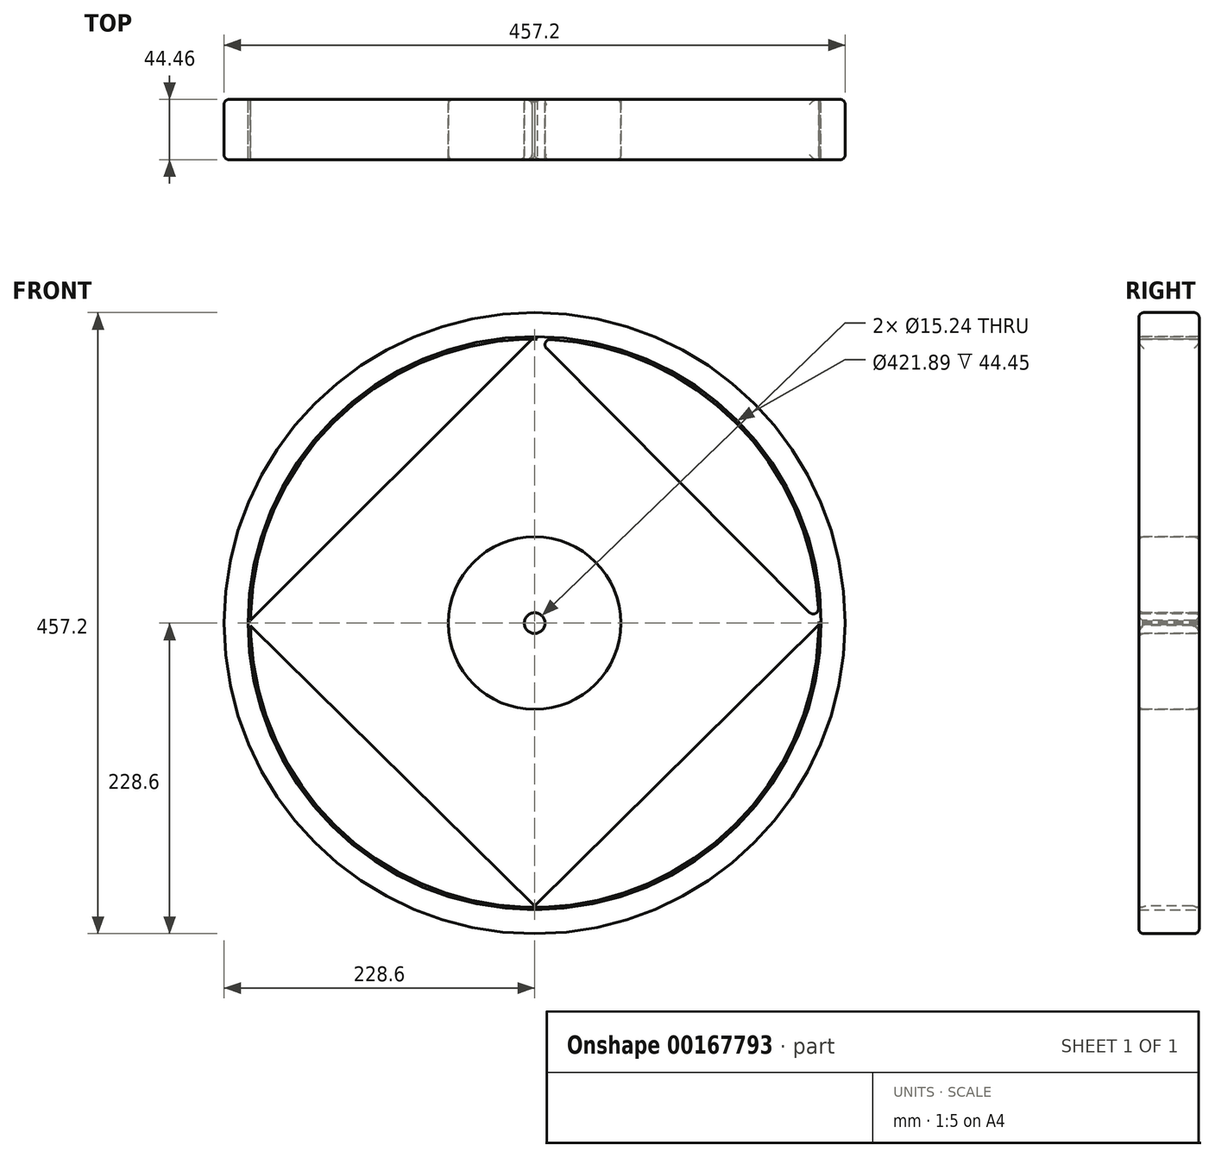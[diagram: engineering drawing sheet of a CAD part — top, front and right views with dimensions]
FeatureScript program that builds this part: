
annotation { "Feature Type Name" : "Feature", "Feature Type Description" : "" }
export const myFeature = defineFeature(function(context is Context, id is Id, definition is map)
    precondition{}
    {
        {
            var Q0;
            Q0=qCreatedBy(makeId("Front.planeOp"),FACE);
            var sketch = newSketch(context, id + "F0", { "sketchPlane" : qUnion([Q0])});
            skCircle(sketch, "E0", {"center": v(0, 0) * mm, "radius": 228.6 * mm});
            skCircle(sketch, "E1", {"center": v(0, 0) * mm, "radius": 7.62 * mm});
            skLineSegment(sketch, "E2", {"start": v(0, 0) * mm, "end": v(0, 228.6) * mm});
            skLineSegment(sketch, "E3", {"start": v(0, 0) * mm, "end": v(0, -228.6) * mm});
            skLineSegment(sketch, "E4", {"start": v(0, 0) * mm, "end": v(-228.6, 0) * mm});
            skLineSegment(sketch, "E5", {"start": v(0, 0) * mm, "end": v(228.6, 0) * mm});
            skCircle(sketch, "E6", {"center": v(0, 0) * mm, "radius": 63.5 * mm});
            skCircle(sketch, "E7", {"center": v(0, 0) * mm, "radius": 210.95 * mm});
            skSolve(sketch);
        }
        {
            var Q0;
            Q0=qSketchRegion(id+"F0",true);
            var Q1;
            {var subQ0=sQuery(id+"F0.wireOp",EDGE,"E2");var subQ1=sQuery(id+"F0.wireOp",EDGE,"E0");var subQ2=makeQuery(id+"F0.imprint","INTERSECT",VERTEX,{"derivedFrom":[subQ1,subQ0]});Q1=makeQuery(id+"F0.imprint","IMPRINT",FACE,{"disambiguationData":[TD([[makeQuery(id+"F0.imprint","IMPRINT",EDGE,{"disambiguationData":[TD([[subQ2,-1.0]])],"derivedFrom":subQ1}),1.0]])]});}
            var Q2;
            {var subQ0=sQuery(id+"F0.wireOp",EDGE,"E2");var subQ1=sQuery(id+"F0.wireOp",EDGE,"E1");var subQ2=makeQuery(id+"F0.imprint","INTERSECT",VERTEX,{"derivedFrom":[subQ1,subQ0]});Q2=makeQuery(id+"F0.imprint","IMPRINT",FACE,{"disambiguationData":[TD([[makeQuery(id+"F0.imprint","IMPRINT",EDGE,{"disambiguationData":[TD([[subQ2,-1.0]])],"derivedFrom":subQ1}),-1.0]])]});}
            var Q3;
            {var subQ0=sQuery(id+"F0.wireOp",EDGE,"E2");var subQ1=sQuery(id+"F0.wireOp",EDGE,"E1");var subQ2=makeQuery(id+"F0.imprint","INTERSECT",VERTEX,{"derivedFrom":[subQ1,subQ0]});Q3=makeQuery(id+"F0.imprint","IMPRINT",FACE,{"disambiguationData":[TD([[makeQuery(id+"F0.imprint","IMPRINT",EDGE,{"disambiguationData":[TD([[subQ2,1.0]])],"derivedFrom":subQ1}),-1.0]])]});}
            var Q4;
            {var subQ0=sQuery(id+"F0.wireOp",EDGE,"E5");var subQ1=sQuery(id+"F0.wireOp",EDGE,"E1");var subQ2=makeQuery(id+"F0.imprint","INTERSECT",VERTEX,{"derivedFrom":[subQ1,subQ0]});Q4=makeQuery(id+"F0.imprint","IMPRINT",FACE,{"disambiguationData":[TD([[makeQuery(id+"F0.imprint","IMPRINT",EDGE,{"disambiguationData":[TD([[subQ2,1.0]])],"derivedFrom":subQ1}),-1.0]])]});}
            var Q5;
            {var subQ0=sQuery(id+"F0.wireOp",EDGE,"E4");var subQ1=sQuery(id+"F0.wireOp",EDGE,"E1");var subQ2=makeQuery(id+"F0.imprint","INTERSECT",VERTEX,{"derivedFrom":[subQ1,subQ0]});Q5=makeQuery(id+"F0.imprint","IMPRINT",FACE,{"disambiguationData":[TD([[makeQuery(id+"F0.imprint","IMPRINT",EDGE,{"disambiguationData":[TD([[subQ2,-1.0]])],"derivedFrom":subQ1}),-1.0]])]});}
            extrude(context, id + "F1", {"entities" : qUnion([Q0, Q1, Q2, Q3, Q4, Q5]), "endBound" : BoundingType.SYMMETRIC, "depth" : 44.45 * mm});
        }
        {
            var Q0;
            Q0=makeQuery(id+"F1.opExtrude","CAP_FACE",FACE,{"disambiguationData":[OSD([sQuery(id+"F0.wireOp",EDGE,"E1"),sQuery(id+"F0.wireOp",EDGE,"E6")])],"isStart":false});
            var sketch = newSketch(context, id + "F2", { "sketchPlane" : qUnion([Q0])});
            skLineSegment(sketch, "E8", {"start": v(-209.14, 0) * mm, "end": v(-211.01, 0) * mm});
            skLineSegment(sketch, "E9", {"start": v(209.14, 0) * mm, "end": v(210.23, 0) * mm});
            skLineSegment(sketch, "E10", {"start": v(0, 209.14) * mm, "end": v(0, 211.07) * mm});
            skLineSegment(sketch, "E11", {"start": v(0, -208.2) * mm, "end": v(-211.01, 0) * mm});
            skLineSegment(sketch, "E12", {"start": v(-211.01, 0) * mm, "end": v(0, 211.07) * mm});
            skLineSegment(sketch, "E13", {"start": v(0, 211.07) * mm, "end": v(210.23, 0) * mm});
            skLineSegment(sketch, "E14", {"start": v(210.23, 0) * mm, "end": v(0, -208.2) * mm});
            skCircle(sketch, "E15", {"center": v(0, 0) * mm, "radius": 209.14 * mm});
            skSolve(sketch);
        }
        {
            var Q0;
            {var subQ0=sQuery(id+"F2.wireOp",EDGE,"E14");var subQ1=sQuery(id+"F2.wireOp",EDGE,"E11");var subQ2=makeQuery(id+"F2.imprint","INTERSECT",VERTEX,{"derivedFrom":[subQ1,subQ0]});Q0=makeQuery(id+"F2.imprint","IMPRINT",FACE,{"disambiguationData":[TD([[makeQuery(id+"F2.imprint","IMPRINT",EDGE,{"disambiguationData":[TD([[subQ2,-1.0]])],"derivedFrom":subQ1}),1.0]])]});}
            var Q1;
            {var subQ0=sQuery(id+"F2.wireOp",EDGE,"E15");var subQ1=sQuery(id+"F2.wireOp",EDGE,"E12");var subQ2=makeQuery(id+"F2.imprint","INTERSECT",VERTEX,{"disambiguationData":[OD(0.0)],"derivedFrom":[subQ1,subQ0]});Q1=makeQuery(id+"F2.imprint","IMPRINT",FACE,{"disambiguationData":[TD([[makeQuery(id+"F2.imprint","IMPRINT",EDGE,{"disambiguationData":[TD([[subQ2,-1.0]])],"derivedFrom":subQ1}),1.0]])]});}
            var Q2;
            {var subQ0=sQuery(id+"F2.wireOp",EDGE,"E15");var subQ1=sQuery(id+"F2.wireOp",EDGE,"E13");var subQ2=makeQuery(id+"F2.imprint","INTERSECT",VERTEX,{"disambiguationData":[OD(0.0)],"derivedFrom":[subQ1,subQ0]});Q2=makeQuery(id+"F2.imprint","IMPRINT",FACE,{"disambiguationData":[TD([[makeQuery(id+"F2.imprint","IMPRINT",EDGE,{"disambiguationData":[TD([[subQ2,-1.0]])],"derivedFrom":subQ1}),1.0]])]});}
            var Q3;
            {var subQ0=sQuery(id+"F2.wireOp",EDGE,"E8");Q3=makeQuery(id+"F2.imprint","IMPRINT",FACE,{"disambiguationData":[TD([[makeQuery(id+"F2.imprint","IMPRINT",EDGE,{"derivedFrom":subQ0}),1.0]])]});}
            var Q4;
            {var subQ0=sQuery(id+"F2.wireOp",EDGE,"E8");Q4=makeQuery(id+"F2.imprint","IMPRINT",FACE,{"disambiguationData":[TD([[makeQuery(id+"F2.imprint","IMPRINT",EDGE,{"derivedFrom":subQ0}),-1.0]])]});}
            var Q5;
            {var subQ0=sQuery(id+"F2.wireOp",EDGE,"E9");Q5=makeQuery(id+"F2.imprint","IMPRINT",FACE,{"disambiguationData":[TD([[makeQuery(id+"F2.imprint","IMPRINT",EDGE,{"derivedFrom":subQ0}),1.0]])]});}
            var Q6;
            {var subQ0=sQuery(id+"F2.wireOp",EDGE,"E9");Q6=makeQuery(id+"F2.imprint","IMPRINT",FACE,{"disambiguationData":[TD([[makeQuery(id+"F2.imprint","IMPRINT",EDGE,{"derivedFrom":subQ0}),-1.0]])]});}
            var Q7;
            {var subQ0=sQuery(id+"F2.wireOp",EDGE,"E10");Q7=makeQuery(id+"F2.imprint","IMPRINT",FACE,{"disambiguationData":[TD([[makeQuery(id+"F2.imprint","IMPRINT",EDGE,{"derivedFrom":subQ0}),1.0]])]});}
            var Q8;
            {var subQ0=sQuery(id+"F2.wireOp",EDGE,"E10");Q8=makeQuery(id+"F2.imprint","IMPRINT",FACE,{"disambiguationData":[TD([[makeQuery(id+"F2.imprint","IMPRINT",EDGE,{"derivedFrom":subQ0}),-1.0]])]});}
            var Q9;
            Q9=makeQuery(id+"F2.imprint","IMPRINT",FACE,{"disambiguationData":[TD([[makeQuery(id+"F2.imprint","IMPRINT",EDGE,{"derivedFrom":makeQuery(id+"F1.opExtrude","CAP_EDGE",EDGE,{"disambiguationData":[OSD([sQuery(id+"F0.wireOp",EDGE,"E1")])],"isStart":false})}),-1.0]])]});
            extrude(context, id + "F3", {"entities" : qUnion([Q0, Q1, Q2, Q3, Q4, Q5, Q6, Q7, Q8, Q9]), "oppositeDirection" : true, "depth" : 44.45 * mm});
        }
        {
            var Q0;
            {var subQ0=sQuery(id+"F2.wireOp",EDGE,"E15");var subQ1=sQuery(id+"F2.wireOp",EDGE,"E13");Q0=makeQuery(id+"F3.opExtrude","SWEPT_EDGE",EDGE,{"disambiguationData":[OSD([subQ1,subQ0]),TDD([makeQuery(id+"F2.imprint","INTERSECT",VERTEX,{"disambiguationData":[OD(1.0)],"derivedFrom":[subQ1,subQ0]})]),ownerDisambiguation([makeQuery(id+"F3.opExtrude","SWEPT_BODY",BODY,{"disambiguationData":[OSD([subQ1,subQ0])]})])]});}
            var Q1;
            {var subQ0=sQuery(id+"F2.wireOp",EDGE,"E15");var subQ1=sQuery(id+"F2.wireOp",EDGE,"E13");Q1=makeQuery(id+"F3.opExtrude","SWEPT_EDGE",EDGE,{"disambiguationData":[OSD([subQ1,subQ0]),TDD([makeQuery(id+"F2.imprint","INTERSECT",VERTEX,{"disambiguationData":[OD(0.0)],"derivedFrom":[subQ1,subQ0]})]),ownerDisambiguation([makeQuery(id+"F3.opExtrude","SWEPT_BODY",BODY,{"disambiguationData":[OSD([subQ1,subQ0])]})])]});}
            var Q2;
            {var subQ0=sQuery(id+"F2.wireOp",EDGE,"E15");var subQ1=sQuery(id+"F2.wireOp",EDGE,"E11");Q2=makeQuery(id+"F3.opExtrude","SWEPT_EDGE",EDGE,{"disambiguationData":[OSD([subQ1,subQ0]),ownerDisambiguation([makeQuery(id+"F3.opExtrude","SWEPT_BODY",BODY,{"disambiguationData":[OSD([subQ1,sQuery(id+"F2.wireOp",EDGE,"E14"),subQ0])]})])]});}
            var Q3;
            Q3=makeQuery(id+"F3.opExtrude","SWEPT_EDGE",EDGE,{"disambiguationData":[OSD([sQuery(id+"F2.wireOp",EDGE,"E11"),sQuery(id+"F2.wireOp",EDGE,"E14")])]});
            var Q4;
            Q4=makeQuery(id+"F1.opExtrude","CAP_EDGE",EDGE,{"disambiguationData":[OSD([sQuery(id+"F0.wireOp",EDGE,"E6")])],"isStart":true});
            var Q5;
            Q5=makeQuery(id+"F3.opExtrude","CAP_EDGE",EDGE,{"disambiguationData":[OSD([sQuery(id+"F0.wireOp",EDGE,"E6")])],"isStart":true});
            var Q6;
            Q6=makeQuery(id+"F3.opExtrude","CAP_FACE",FACE,{"disambiguationData":[OSD([sQuery(id+"F0.wireOp",EDGE,"E6")])],"isStart":true});
            var Q7;
            Q7=makeQuery(id+"F1.opExtrude","CAP_EDGE",EDGE,{"disambiguationData":[OSD([sQuery(id+"F0.wireOp",EDGE,"E0")])],"isStart":false});
            var Q8;
            Q8=makeQuery(id+"F1.opExtrude","CAP_EDGE",EDGE,{"disambiguationData":[OSD([sQuery(id+"F0.wireOp",EDGE,"E0")])],"isStart":true});
            var Q9;
            {var subQ0=sQuery(id+"F2.wireOp",EDGE,"E15");var subQ1=sQuery(id+"F2.wireOp",EDGE,"E12");Q9=makeQuery(id+"F3.opExtrude","CAP_EDGE",EDGE,{"disambiguationData":[OSD([subQ1]),TDD([makeQuery(id+"F2.imprint","IMPRINT",EDGE,{"disambiguationData":[TD([[makeQuery(id+"F2.imprint","INTERSECT",VERTEX,{"disambiguationData":[OD(0.0)],"derivedFrom":[subQ1,subQ0]}),-1.0]])],"derivedFrom":subQ1})])],"isStart":true});}
            var Q10;
            {var subQ0=sQuery(id+"F2.wireOp",EDGE,"E15");var subQ1=sQuery(id+"F2.wireOp",EDGE,"E13");Q10=makeQuery(id+"F3.opExtrude","CAP_EDGE",EDGE,{"disambiguationData":[OSD([subQ1]),TDD([makeQuery(id+"F2.imprint","IMPRINT",EDGE,{"disambiguationData":[TD([[makeQuery(id+"F2.imprint","INTERSECT",VERTEX,{"disambiguationData":[OD(0.0)],"derivedFrom":[subQ1,subQ0]}),-1.0]])],"derivedFrom":subQ1})])],"isStart":true});}
            var Q11;
            {var subQ0=sQuery(id+"F2.wireOp",EDGE,"E14");Q11=makeQuery(id+"F3.opExtrude","CAP_EDGE",EDGE,{"disambiguationData":[OSD([subQ0]),TDD([makeQuery(id+"F2.imprint","IMPRINT",EDGE,{"disambiguationData":[TD([[makeQuery(id+"F2.imprint","INTERSECT",VERTEX,{"derivedFrom":[sQuery(id+"F2.wireOp",EDGE,"E11"),subQ0]}),1.0]])],"derivedFrom":subQ0})])],"isStart":true});}
            var Q12;
            {var subQ0=sQuery(id+"F2.wireOp",EDGE,"E11");Q12=makeQuery(id+"F3.opExtrude","CAP_EDGE",EDGE,{"disambiguationData":[OSD([subQ0]),TDD([makeQuery(id+"F2.imprint","IMPRINT",EDGE,{"disambiguationData":[TD([[makeQuery(id+"F2.imprint","INTERSECT",VERTEX,{"derivedFrom":[subQ0,sQuery(id+"F2.wireOp",EDGE,"E14")]}),-1.0]])],"derivedFrom":subQ0})])],"isStart":true});}
            var Q13;
            {var subQ0=sQuery(id+"F2.wireOp",EDGE,"E15");var subQ1=sQuery(id+"F2.wireOp",EDGE,"E13");Q13=makeQuery(id+"F3.opExtrude","CAP_EDGE",EDGE,{"disambiguationData":[OSD([subQ1]),TDD([makeQuery(id+"F2.imprint","IMPRINT",EDGE,{"disambiguationData":[TD([[makeQuery(id+"F2.imprint","INTERSECT",VERTEX,{"disambiguationData":[OD(0.0)],"derivedFrom":[subQ1,subQ0]}),-1.0]])],"derivedFrom":subQ1})])],"isStart":false});}
            var Q14;
            {var subQ0=sQuery(id+"F2.wireOp",EDGE,"E11");Q14=makeQuery(id+"F3.opExtrude","CAP_EDGE",EDGE,{"disambiguationData":[OSD([subQ0]),TDD([makeQuery(id+"F2.imprint","IMPRINT",EDGE,{"disambiguationData":[TD([[makeQuery(id+"F2.imprint","INTERSECT",VERTEX,{"derivedFrom":[subQ0,sQuery(id+"F2.wireOp",EDGE,"E14")]}),-1.0]])],"derivedFrom":subQ0})])],"isStart":false});}
            var Q15;
            {var subQ0=sQuery(id+"F2.wireOp",EDGE,"E14");Q15=makeQuery(id+"F3.opExtrude","CAP_EDGE",EDGE,{"disambiguationData":[OSD([subQ0]),TDD([makeQuery(id+"F2.imprint","IMPRINT",EDGE,{"disambiguationData":[TD([[makeQuery(id+"F2.imprint","INTERSECT",VERTEX,{"derivedFrom":[sQuery(id+"F2.wireOp",EDGE,"E11"),subQ0]}),1.0]])],"derivedFrom":subQ0})])],"isStart":false});}
            var Q16;
            {var subQ0=sQuery(id+"F2.wireOp",EDGE,"E15");var subQ1=sQuery(id+"F2.wireOp",EDGE,"E12");Q16=makeQuery(id+"F3.opExtrude","CAP_EDGE",EDGE,{"disambiguationData":[OSD([subQ1]),TDD([makeQuery(id+"F2.imprint","IMPRINT",EDGE,{"disambiguationData":[TD([[makeQuery(id+"F2.imprint","INTERSECT",VERTEX,{"disambiguationData":[OD(0.0)],"derivedFrom":[subQ1,subQ0]}),-1.0]])],"derivedFrom":subQ1})])],"isStart":false});}
            fillet(context, id + "F4", {"entities" : qUnion([Q0, Q1, Q2, Q3, Q4, Q5, Q6, Q7, Q8, Q9, Q10, Q11, Q12, Q13, Q14, Q15, Q16]), "radius" : 3.8 * mm, "tangentPropagation" : true, "allowEdgeOverflow" : false});
        }
        {
            var Q0;
            {var subQ0=sQuery(id+"F2.wireOp",EDGE,"E15");var subQ1=sQuery(id+"F2.wireOp",EDGE,"E13");Q0=makeQuery(id+"F3.opExtrude","CAP_EDGE",EDGE,{"disambiguationData":[OSD([subQ1]),TDD([makeQuery(id+"F2.imprint","IMPRINT",EDGE,{"disambiguationData":[TD([[makeQuery(id+"F2.imprint","INTERSECT",VERTEX,{"disambiguationData":[OD(0.0)],"derivedFrom":[subQ1,subQ0]}),-1.0]])],"derivedFrom":subQ1})])],"isStart":true});}
            var Q1;
            {var subQ0=sQuery(id+"F2.wireOp",EDGE,"E14");Q1=makeQuery(id+"F3.opExtrude","CAP_EDGE",EDGE,{"disambiguationData":[OSD([subQ0]),TDD([makeQuery(id+"F2.imprint","IMPRINT",EDGE,{"disambiguationData":[TD([[makeQuery(id+"F2.imprint","INTERSECT",VERTEX,{"derivedFrom":[sQuery(id+"F2.wireOp",EDGE,"E11"),subQ0]}),1.0]])],"derivedFrom":subQ0})])],"isStart":true});}
            var Q2;
            {var subQ0=sQuery(id+"F2.wireOp",EDGE,"E11");Q2=makeQuery(id+"F3.opExtrude","CAP_EDGE",EDGE,{"disambiguationData":[OSD([subQ0]),TDD([makeQuery(id+"F2.imprint","IMPRINT",EDGE,{"disambiguationData":[TD([[makeQuery(id+"F2.imprint","INTERSECT",VERTEX,{"derivedFrom":[subQ0,sQuery(id+"F2.wireOp",EDGE,"E14")]}),-1.0]])],"derivedFrom":subQ0})])],"isStart":true});}
            var Q3;
            {var subQ0=sQuery(id+"F2.wireOp",EDGE,"E15");var subQ1=sQuery(id+"F2.wireOp",EDGE,"E12");Q3=makeQuery(id+"F3.opExtrude","CAP_EDGE",EDGE,{"disambiguationData":[OSD([subQ1]),TDD([makeQuery(id+"F2.imprint","IMPRINT",EDGE,{"disambiguationData":[TD([[makeQuery(id+"F2.imprint","INTERSECT",VERTEX,{"disambiguationData":[OD(0.0)],"derivedFrom":[subQ1,subQ0]}),-1.0]])],"derivedFrom":subQ1})])],"isStart":true});}
            var Q4;
            Q4=makeQuery(id+"F1.opExtrude","CAP_EDGE",EDGE,{"disambiguationData":[OSD([sQuery(id+"F0.wireOp",EDGE,"E0")])],"isStart":false});
            var Q5;
            Q5=makeQuery(id+"F1.opExtrude","CAP_EDGE",EDGE,{"disambiguationData":[OSD([sQuery(id+"F0.wireOp",EDGE,"E0")])],"isStart":true});
            var Q6;
            {var subQ0=sQuery(id+"F2.wireOp",EDGE,"E14");Q6=makeQuery(id+"F3.opExtrude","CAP_EDGE",EDGE,{"disambiguationData":[OSD([subQ0]),TDD([makeQuery(id+"F2.imprint","IMPRINT",EDGE,{"disambiguationData":[TD([[makeQuery(id+"F2.imprint","INTERSECT",VERTEX,{"derivedFrom":[sQuery(id+"F2.wireOp",EDGE,"E11"),subQ0]}),1.0]])],"derivedFrom":subQ0})])],"isStart":false});}
            var Q7;
            Q7=makeQuery(id+"F1.opExtrude","CAP_EDGE",EDGE,{"disambiguationData":[OSD([sQuery(id+"F0.wireOp",EDGE,"E6")])],"isStart":true});
            var Q8;
            {var subQ0=sQuery(id+"F2.wireOp",EDGE,"E15");var subQ1=sQuery(id+"F2.wireOp",EDGE,"E12");Q8=makeQuery(id+"F3.opExtrude","CAP_EDGE",EDGE,{"disambiguationData":[OSD([subQ1]),TDD([makeQuery(id+"F2.imprint","IMPRINT",EDGE,{"disambiguationData":[TD([[makeQuery(id+"F2.imprint","INTERSECT",VERTEX,{"disambiguationData":[OD(0.0)],"derivedFrom":[subQ1,subQ0]}),-1.0]])],"derivedFrom":subQ1})])],"isStart":false});}
            var Q9;
            {var subQ0=sQuery(id+"F2.wireOp",EDGE,"E11");Q9=makeQuery(id+"F3.opExtrude","CAP_EDGE",EDGE,{"disambiguationData":[OSD([subQ0]),TDD([makeQuery(id+"F2.imprint","IMPRINT",EDGE,{"disambiguationData":[TD([[makeQuery(id+"F2.imprint","INTERSECT",VERTEX,{"derivedFrom":[subQ0,sQuery(id+"F2.wireOp",EDGE,"E14")]}),-1.0]])],"derivedFrom":subQ0})])],"isStart":false});}
            fillet(context, id + "F5", {"entities" : qUnion([Q0, Q1, Q2, Q3, Q4, Q5, Q6, Q7, Q8, Q9]), "radius" : 5.08 * mm, "tangentPropagation" : true, "allowEdgeOverflow" : false});
        }
    });
